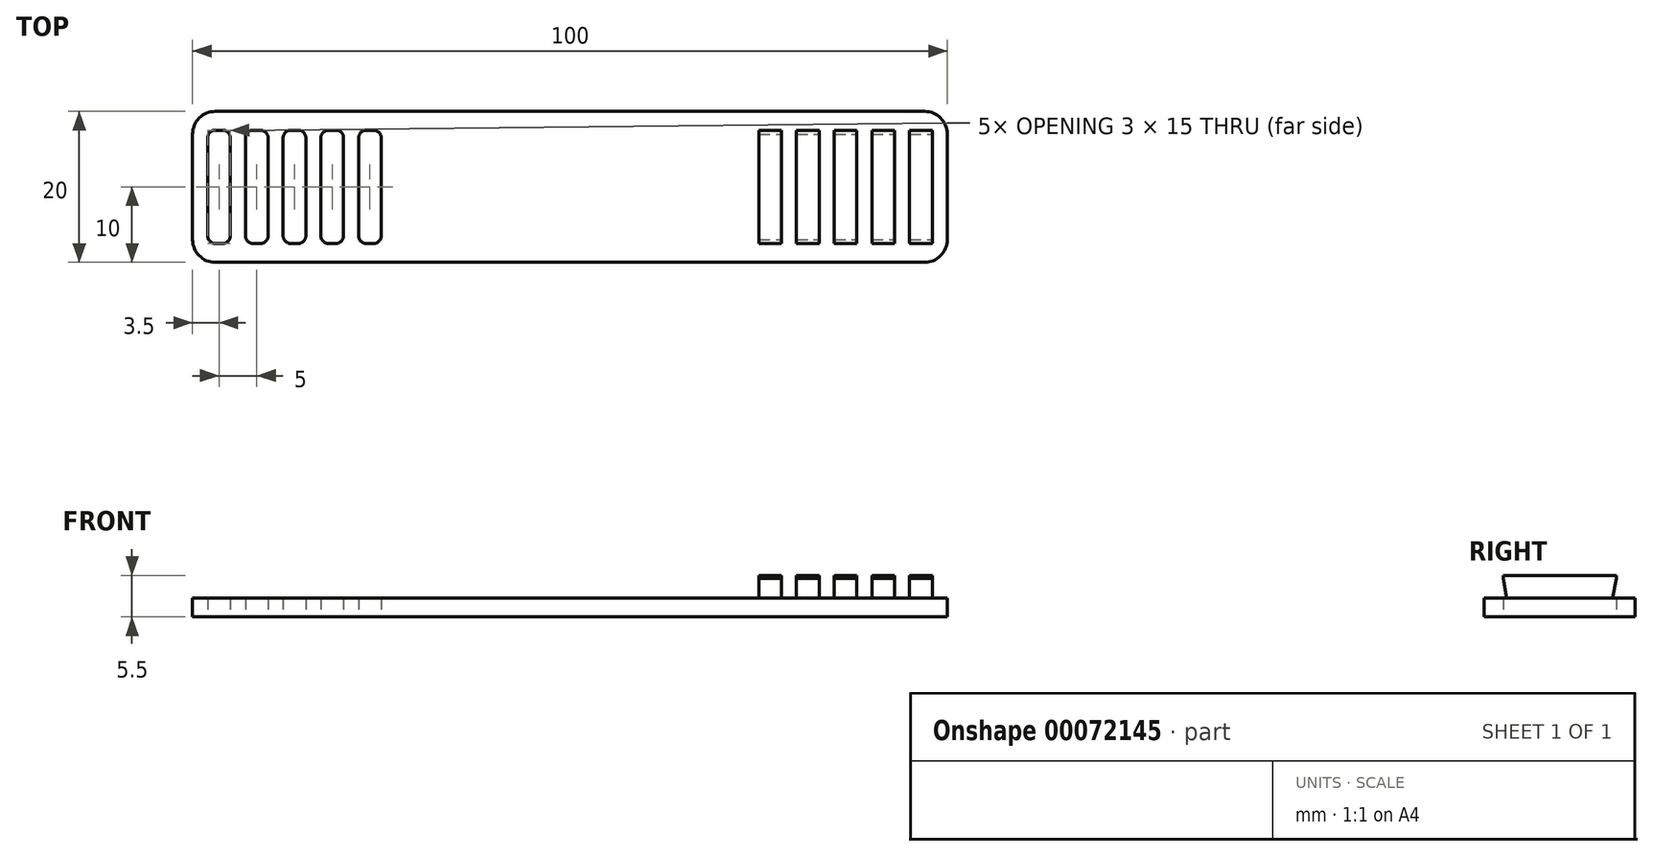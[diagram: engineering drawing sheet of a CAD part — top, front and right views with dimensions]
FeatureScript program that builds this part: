
annotation { "Feature Type Name" : "Feature", "Feature Type Description" : "" }
export const myFeature = defineFeature(function(context is Context, id is Id, definition is map)
    precondition{}
    {
        {
            var Q0;
            Q0=qCreatedBy(makeId("Top.planeOp"),FACE);
            var sketch = newSketch(context, id + "F0", { "sketchPlane" : qUnion([Q0])});
            skLineSegment(sketch, "E0.rect.bottom", {"start": v(50, -10) * mm, "end": v(-50, -10) * mm});
            skLineSegment(sketch, "E0.rect.top", {"start": v(50, 10) * mm, "end": v(-50, 10) * mm});
            skLineSegment(sketch, "E0.rect.left", {"start": v(50, -10) * mm, "end": v(50, 10) * mm});
            skLineSegment(sketch, "E0.rect.right", {"start": v(-50, -10) * mm, "end": v(-50, 10) * mm});
            skPoint(sketch, "E0.rect.middle", {"position": v(0, 0) * mm});
            skLineSegment(sketch, "E1", {"start": v(0, 10) * mm, "end": v(0, -10) * mm, "construction": true});
            skLineSegment(sketch, "E2", {"start": v(-50, 0) * mm, "end": v(50, 0) * mm, "construction": true});
            skLineSegment(sketch, "E3.rect.bottom", {"start": v(-46, -7.5) * mm, "end": v(-47, -7.5) * mm});
            skLineSegment(sketch, "E3.rect.top", {"start": v(-46, 7.5) * mm, "end": v(-47, 7.5) * mm});
            skLineSegment(sketch, "E3.rect.left", {"start": v(-45, -6.5) * mm, "end": v(-45, 6.5) * mm});
            skLineSegment(sketch, "E3.rect.right", {"start": v(-48, -6.5) * mm, "end": v(-48, 6.5) * mm});
            skPoint(sketch, "E3.rect.middle", {"position": v(-46.5, 0) * mm});
            skLineSegment(sketch, "E4.1.0.0", {"start": v(-41, 7.5) * mm, "end": v(-42, 7.5) * mm});
            skLineSegment(sketch, "E4.1.0.1", {"start": v(-40, -6.5) * mm, "end": v(-40, 6.5) * mm});
            skLineSegment(sketch, "E4.1.0.2", {"start": v(-41, -7.5) * mm, "end": v(-42, -7.5) * mm});
            skLineSegment(sketch, "E4.1.0.3", {"start": v(-43, -6.5) * mm, "end": v(-43, 6.5) * mm});
            skLineSegment(sketch, "E4.2.0.0", {"start": v(-36, 7.5) * mm, "end": v(-37, 7.5) * mm});
            skLineSegment(sketch, "E4.2.0.1", {"start": v(-35, -6.5) * mm, "end": v(-35, 6.5) * mm});
            skLineSegment(sketch, "E4.2.0.2", {"start": v(-36, -7.5) * mm, "end": v(-37, -7.5) * mm});
            skLineSegment(sketch, "E4.2.0.3", {"start": v(-38, -6.5) * mm, "end": v(-38, 6.5) * mm});
            skLineSegment(sketch, "E4.3.0.0", {"start": v(-31, 7.5) * mm, "end": v(-32, 7.5) * mm});
            skLineSegment(sketch, "E4.3.0.1", {"start": v(-30, -6.5) * mm, "end": v(-30, 6.5) * mm});
            skLineSegment(sketch, "E4.3.0.2", {"start": v(-31, -7.5) * mm, "end": v(-32, -7.5) * mm});
            skLineSegment(sketch, "E4.3.0.3", {"start": v(-33, -6.5) * mm, "end": v(-33, 6.5) * mm});
            skLineSegment(sketch, "E4.4.0.0", {"start": v(-26, 7.5) * mm, "end": v(-27, 7.5) * mm});
            skLineSegment(sketch, "E4.4.0.1", {"start": v(-25, -6.5) * mm, "end": v(-25, 6.5) * mm});
            skLineSegment(sketch, "E4.4.0.2", {"start": v(-26, -7.5) * mm, "end": v(-27, -7.5) * mm});
            skLineSegment(sketch, "E4.4.0.3", {"start": v(-28, -6.5) * mm, "end": v(-28, 6.5) * mm});
            skLineSegment(sketch, "E4.direction1", {"start": v(-48, 7.5) * mm, "end": v(-43, 7.5) * mm, "construction": true});
            skLineSegment(sketch, "E5.MirrorCS", {"start": v(48, 7.5) * mm, "end": v(43, 7.5) * mm, "construction": true});
            skLineSegment(sketch, "E6.MirrorCS", {"start": v(30, 7.5) * mm, "end": v(33, 7.5) * mm});
            skLineSegment(sketch, "E7.MirrorCS", {"start": v(25, 7.5) * mm, "end": v(28, 7.5) * mm});
            skLineSegment(sketch, "E8.MirrorCS", {"start": v(28, -7.5) * mm, "end": v(28, 7.5) * mm});
            skLineSegment(sketch, "E9.MirrorCS", {"start": v(38, -7.5) * mm, "end": v(38, 7.5) * mm});
            skLineSegment(sketch, "E10.MirrorCS", {"start": v(33, -7.5) * mm, "end": v(33, 7.5) * mm});
            skLineSegment(sketch, "E11.MirrorCS", {"start": v(25, -7.5) * mm, "end": v(28, -7.5) * mm});
            skPoint(sketch, "E12.MirrorP", {"position": v(46.5, 0) * mm});
            skLineSegment(sketch, "E13.MirrorCS", {"start": v(35, -7.5) * mm, "end": v(38, -7.5) * mm});
            skLineSegment(sketch, "E14.MirrorCS", {"start": v(30, -7.5) * mm, "end": v(33, -7.5) * mm});
            skLineSegment(sketch, "E15.MirrorCS", {"start": v(25, -7.5) * mm, "end": v(25, 7.5) * mm});
            skLineSegment(sketch, "E16.MirrorCS", {"start": v(40, -7.5) * mm, "end": v(43, -7.5) * mm});
            skLineSegment(sketch, "E17.MirrorCS", {"start": v(40, -7.5) * mm, "end": v(40, 7.5) * mm});
            skLineSegment(sketch, "E18.MirrorCS", {"start": v(40, 7.5) * mm, "end": v(43, 7.5) * mm});
            skLineSegment(sketch, "E19.MirrorCS", {"start": v(48, -7.5) * mm, "end": v(48, 7.5) * mm});
            skLineSegment(sketch, "E20.MirrorCS", {"start": v(45, -7.5) * mm, "end": v(45, 7.5) * mm});
            skLineSegment(sketch, "E21.MirrorCS", {"start": v(45, 7.5) * mm, "end": v(48, 7.5) * mm});
            skLineSegment(sketch, "E22.MirrorCS", {"start": v(45, -7.5) * mm, "end": v(48, -7.5) * mm});
            skLineSegment(sketch, "E23.MirrorCS", {"start": v(30, -7.5) * mm, "end": v(30, 7.5) * mm});
            skLineSegment(sketch, "E24.MirrorCS", {"start": v(43, -7.5) * mm, "end": v(43, 7.5) * mm});
            skLineSegment(sketch, "E25.MirrorCS", {"start": v(35, 7.5) * mm, "end": v(38, 7.5) * mm});
            skLineSegment(sketch, "E26.MirrorCS", {"start": v(35, -7.5) * mm, "end": v(35, 7.5) * mm});
            skPoint(sketch, "E27.visualSharp", {"position": v(-48, 7.5) * mm});
            skArc(sketch, "E27.filletArc", {"start": v(-47, 7.5) * mm, "mid": v(-47.7, 7.2) * mm, "end": v(-48, 6.5) * mm});
            skPoint(sketch, "E28.visualSharp", {"position": v(-45, 7.5) * mm});
            skArc(sketch, "E28.filletArc", {"start": v(-45, 6.5) * mm, "mid": v(-45.3, 7.2) * mm, "end": v(-46, 7.5) * mm});
            skPoint(sketch, "E29.visualSharp", {"position": v(-45, -7.5) * mm});
            skArc(sketch, "E29.filletArc", {"start": v(-46, -7.5) * mm, "mid": v(-45.3, -7.2) * mm, "end": v(-45, -6.5) * mm});
            skPoint(sketch, "E30.visualSharp", {"position": v(-48, -7.5) * mm});
            skArc(sketch, "E30.filletArc", {"start": v(-48, -6.5) * mm, "mid": v(-47.7, -7.2) * mm, "end": v(-47, -7.5) * mm});
            skPoint(sketch, "E31.visualSharp", {"position": v(-43, 7.5) * mm});
            skArc(sketch, "E31.filletArc", {"start": v(-42, 7.5) * mm, "mid": v(-42.7, 7.2) * mm, "end": v(-43, 6.5) * mm});
            skPoint(sketch, "E32.visualSharp", {"position": v(-40, 7.5) * mm});
            skArc(sketch, "E32.filletArc", {"start": v(-40, 6.5) * mm, "mid": v(-40.3, 7.2) * mm, "end": v(-41, 7.5) * mm});
            skPoint(sketch, "E33.visualSharp", {"position": v(-38, 7.5) * mm});
            skArc(sketch, "E33.filletArc", {"start": v(-37, 7.5) * mm, "mid": v(-37.7, 7.2) * mm, "end": v(-38, 6.5) * mm});
            skPoint(sketch, "E34.visualSharp", {"position": v(-35, 7.5) * mm});
            skArc(sketch, "E34.filletArc", {"start": v(-35, 6.5) * mm, "mid": v(-35.3, 7.2) * mm, "end": v(-36, 7.5) * mm});
            skPoint(sketch, "E35.visualSharp", {"position": v(-33, 7.5) * mm});
            skArc(sketch, "E35.filletArc", {"start": v(-32, 7.5) * mm, "mid": v(-32.7, 7.2) * mm, "end": v(-33, 6.5) * mm});
            skPoint(sketch, "E36.visualSharp", {"position": v(-30, 7.5) * mm});
            skArc(sketch, "E36.filletArc", {"start": v(-30, 6.5) * mm, "mid": v(-30.3, 7.2) * mm, "end": v(-31, 7.5) * mm});
            skPoint(sketch, "E37.visualSharp", {"position": v(-28, 7.5) * mm});
            skArc(sketch, "E37.filletArc", {"start": v(-27, 7.5) * mm, "mid": v(-27.7, 7.2) * mm, "end": v(-28, 6.5) * mm});
            skPoint(sketch, "E38.visualSharp", {"position": v(-25, 7.5) * mm});
            skArc(sketch, "E38.filletArc", {"start": v(-25, 6.5) * mm, "mid": v(-25.3, 7.2) * mm, "end": v(-26, 7.5) * mm});
            skPoint(sketch, "E39.visualSharp", {"position": v(-25, -7.5) * mm});
            skArc(sketch, "E39.filletArc", {"start": v(-26, -7.5) * mm, "mid": v(-25.3, -7.2) * mm, "end": v(-25, -6.5) * mm});
            skPoint(sketch, "E40.visualSharp", {"position": v(-28, -7.5) * mm});
            skArc(sketch, "E40.filletArc", {"start": v(-28, -6.5) * mm, "mid": v(-27.7, -7.2) * mm, "end": v(-27, -7.5) * mm});
            skPoint(sketch, "E41.visualSharp", {"position": v(-30, -7.5) * mm});
            skArc(sketch, "E41.filletArc", {"start": v(-31, -7.5) * mm, "mid": v(-30.3, -7.2) * mm, "end": v(-30, -6.5) * mm});
            skPoint(sketch, "E42.visualSharp", {"position": v(-33, -7.5) * mm});
            skArc(sketch, "E42.filletArc", {"start": v(-33, -6.5) * mm, "mid": v(-32.7, -7.2) * mm, "end": v(-32, -7.5) * mm});
            skPoint(sketch, "E43.visualSharp", {"position": v(-35, -7.5) * mm});
            skArc(sketch, "E43.filletArc", {"start": v(-36, -7.5) * mm, "mid": v(-35.3, -7.2) * mm, "end": v(-35, -6.5) * mm});
            skPoint(sketch, "E44.visualSharp", {"position": v(-38, -7.5) * mm});
            skArc(sketch, "E44.filletArc", {"start": v(-38, -6.5) * mm, "mid": v(-37.7, -7.2) * mm, "end": v(-37, -7.5) * mm});
            skPoint(sketch, "E45.visualSharp", {"position": v(-40, -7.5) * mm});
            skArc(sketch, "E45.filletArc", {"start": v(-41, -7.5) * mm, "mid": v(-40.3, -7.2) * mm, "end": v(-40, -6.5) * mm});
            skPoint(sketch, "E46.visualSharp", {"position": v(-43, -7.5) * mm});
            skArc(sketch, "E46.filletArc", {"start": v(-43, -6.5) * mm, "mid": v(-42.7, -7.2) * mm, "end": v(-42, -7.5) * mm});
            skSolve(sketch);
        }
        {
            var Q0;
            Q0=makeQuery(id+"F0.imprint","IMPRINT",FACE,{"disambiguationData":[TD([[makeQuery(id+"F0.imprint","IMPRINT",EDGE,{"derivedFrom":sQuery(id+"F0.wireOp",EDGE,"E0.rect.bottom")}),-1.0]])]});
            var Q1;
            Q1=makeQuery(id+"F0.imprint","IMPRINT",FACE,{"disambiguationData":[TD([[makeQuery(id+"F0.imprint","IMPRINT",EDGE,{"derivedFrom":sQuery(id+"F0.wireOp",EDGE,"bae3096f-2a75-4a92-8632-1d8423ab57ea2.MirrorCS")}),-1.0]])]});
            var Q2;
            Q2=makeQuery(id+"F0.imprint","IMPRINT",FACE,{"disambiguationData":[TD([[makeQuery(id+"F0.imprint","IMPRINT",EDGE,{"derivedFrom":sQuery(id+"F0.wireOp",EDGE,"E60.MirrorCS")}),1.0]])]});
            var Q3;
            Q3=makeQuery(id+"F0.imprint","IMPRINT",FACE,{"disambiguationData":[TD([[makeQuery(id+"F0.imprint","IMPRINT",EDGE,{"derivedFrom":sQuery(id+"F0.wireOp",EDGE,"E7.MirrorCS")}),-1.0]])]});
            var Q4;
            Q4=makeQuery(id+"F0.imprint","IMPRINT",FACE,{"disambiguationData":[TD([[makeQuery(id+"F0.imprint","IMPRINT",EDGE,{"derivedFrom":sQuery(id+"F0.wireOp",EDGE,"E6.MirrorCS")}),-1.0]])]});
            var Q5;
            Q5=makeQuery(id+"F0.imprint","IMPRINT",FACE,{"disambiguationData":[TD([[makeQuery(id+"F0.imprint","IMPRINT",EDGE,{"derivedFrom":sQuery(id+"F0.wireOp",EDGE,"E9.MirrorCS")}),1.0]])]});
            var Q6;
            Q6=makeQuery(id+"F0.imprint","IMPRINT",FACE,{"disambiguationData":[TD([[makeQuery(id+"F0.imprint","IMPRINT",EDGE,{"derivedFrom":sQuery(id+"F0.wireOp",EDGE,"E16.MirrorCS")}),1.0]])]});
            var Q7;
            Q7=makeQuery(id+"F0.imprint","IMPRINT",FACE,{"disambiguationData":[TD([[makeQuery(id+"F0.imprint","IMPRINT",EDGE,{"derivedFrom":sQuery(id+"F0.wireOp",EDGE,"E19.MirrorCS")}),1.0]])]});
            extrude(context, id + "F1", {"entities" : qUnion([Q0, Q1, Q2, Q3, Q4, Q5, Q6, Q7]), "depth" : 2.5 * mm});
        }
        {
            var Q0;
            Q0=makeQuery(id+"F1.opExtrude","CAP_FACE",FACE,{"disambiguationData":[OSD([sQuery(id+"F0.wireOp",EDGE,"E0.rect.bottom"),sQuery(id+"F0.wireOp",EDGE,"E0.rect.top"),sQuery(id+"F0.wireOp",EDGE,"E0.rect.left"),sQuery(id+"F0.wireOp",EDGE,"E0.rect.right"),sQuery(id+"F0.wireOp",EDGE,"E3.rect.bottom"),sQuery(id+"F0.wireOp",EDGE,"E3.rect.top"),sQuery(id+"F0.wireOp",EDGE,"E3.rect.left"),sQuery(id+"F0.wireOp",EDGE,"E3.rect.right"),sQuery(id+"F0.wireOp",EDGE,"E4.1.0.0"),sQuery(id+"F0.wireOp",EDGE,"E4.1.0.1"),sQuery(id+"F0.wireOp",EDGE,"E4.1.0.2"),sQuery(id+"F0.wireOp",EDGE,"E4.1.0.3"),sQuery(id+"F0.wireOp",EDGE,"E4.2.0.0"),sQuery(id+"F0.wireOp",EDGE,"E4.2.0.1"),sQuery(id+"F0.wireOp",EDGE,"E4.2.0.2"),sQuery(id+"F0.wireOp",EDGE,"E4.2.0.3"),sQuery(id+"F0.wireOp",EDGE,"E4.3.0.0"),sQuery(id+"F0.wireOp",EDGE,"E4.3.0.1"),sQuery(id+"F0.wireOp",EDGE,"E4.3.0.2"),sQuery(id+"F0.wireOp",EDGE,"E4.3.0.3"),sQuery(id+"F0.wireOp",EDGE,"E4.4.0.0"),sQuery(id+"F0.wireOp",EDGE,"E4.4.0.1"),sQuery(id+"F0.wireOp",EDGE,"E4.4.0.2"),sQuery(id+"F0.wireOp",EDGE,"E4.4.0.3")])],"isStart":false});
            var sketch = newSketch(context, id + "F2", { "sketchPlane" : qUnion([Q0])});
            skLineSegment(sketch, "E47.0", {"start": v(-46, 7.5) * mm, "end": v(-46, 7.5) * mm});
            skLineSegment(sketch, "E48.0", {"start": v(-48, -6.5) * mm, "end": v(-48, 7.5) * mm});
            skLineSegment(sketch, "E49.0", {"start": v(-45, -6.5) * mm, "end": v(-45, 7.5) * mm});
            skLineSegment(sketch, "E50.0", {"start": v(-45, -7.5) * mm, "end": v(-48, -7.5) * mm});
            skLineSegment(sketch, "E51.0", {"start": v(-41, -7.5) * mm, "end": v(-41, -7.5) * mm});
            skLineSegment(sketch, "E52.0", {"start": v(-36, -7.5) * mm, "end": v(-36, -7.5) * mm});
            skLineSegment(sketch, "E53.0", {"start": v(-31, -7.5) * mm, "end": v(-31, -7.5) * mm});
            skLineSegment(sketch, "E54.0", {"start": v(-26, -7.5) * mm, "end": v(-26, -7.5) * mm});
            skLineSegment(sketch, "E55.0", {"start": v(-26, 7.5) * mm, "end": v(-26, 7.5) * mm});
            skLineSegment(sketch, "E56.0", {"start": v(-31, 7.5) * mm, "end": v(-31, 7.5) * mm});
            skLineSegment(sketch, "E57.0", {"start": v(-36, 7.5) * mm, "end": v(-36, 7.5) * mm});
            skLineSegment(sketch, "E58.0", {"start": v(-41, 7.5) * mm, "end": v(-41, 7.5) * mm});
            skLineSegment(sketch, "E59.0", {"start": v(-43, -7.5) * mm, "end": v(-43, 7.5) * mm});
            skLineSegment(sketch, "E60.0", {"start": v(-40, -7.5) * mm, "end": v(-40, 7.5) * mm});
            skLineSegment(sketch, "E61.0", {"start": v(-38, -7.5) * mm, "end": v(-38, 7.5) * mm});
            skLineSegment(sketch, "E62.0", {"start": v(-35, -7.5) * mm, "end": v(-35, 7.5) * mm});
            skLineSegment(sketch, "E63.0", {"start": v(-33, -7.5) * mm, "end": v(-33, 7.5) * mm});
            skLineSegment(sketch, "E64.0", {"start": v(-30, -7.5) * mm, "end": v(-30, 7.5) * mm});
            skLineSegment(sketch, "E65.0", {"start": v(-28, -7.5) * mm, "end": v(-28, 7.5) * mm});
            skLineSegment(sketch, "E66.0", {"start": v(-25, -7.5) * mm, "end": v(-25, 7.5) * mm});
            skLineSegment(sketch, "E67.0", {"start": v(50, 10) * mm, "end": v(-50, 10) * mm});
            skLineSegment(sketch, "E68", {"start": v(0, 10) * mm, "end": v(0, -10) * mm, "construction": true});
            skLineSegment(sketch, "E69.MirrorCS", {"start": v(30, -7.5) * mm, "end": v(33, -7.5) * mm});
            skLineSegment(sketch, "E70.MirrorCS", {"start": v(25, -7.5) * mm, "end": v(28, -7.5) * mm});
            skLineSegment(sketch, "E71.MirrorCS", {"start": v(35, -7.5) * mm, "end": v(38, -7.5) * mm});
            skLineSegment(sketch, "E72.MirrorCS", {"start": v(40, -7.5) * mm, "end": v(43, -7.5) * mm});
            skLineSegment(sketch, "E73.MirrorCS", {"start": v(25, 7.5) * mm, "end": v(28, 7.5) * mm});
            skLineSegment(sketch, "E74.MirrorCS", {"start": v(45, -7.5) * mm, "end": v(48, -7.5) * mm});
            skLineSegment(sketch, "E75.MirrorCS", {"start": v(30, 7.5) * mm, "end": v(33, 7.5) * mm});
            skLineSegment(sketch, "E76.MirrorCS", {"start": v(45, -7.5) * mm, "end": v(45, 7.5) * mm});
            skLineSegment(sketch, "E77.MirrorCS", {"start": v(48, -7.5) * mm, "end": v(48, 7.5) * mm});
            skLineSegment(sketch, "E78.MirrorCS", {"start": v(35, 7.5) * mm, "end": v(38, 7.5) * mm});
            skLineSegment(sketch, "E79.MirrorCS", {"start": v(45, 7.5) * mm, "end": v(48, 7.5) * mm});
            skLineSegment(sketch, "E80.MirrorCS", {"start": v(40, 7.5) * mm, "end": v(43, 7.5) * mm});
            skLineSegment(sketch, "E81.MirrorCS", {"start": v(35, -7.5) * mm, "end": v(35, 7.5) * mm});
            skLineSegment(sketch, "E82.MirrorCS", {"start": v(38, -7.5) * mm, "end": v(38, 7.5) * mm});
            skLineSegment(sketch, "E83.MirrorCS", {"start": v(43, -7.5) * mm, "end": v(43, 7.5) * mm});
            skLineSegment(sketch, "E84.MirrorCS", {"start": v(40, -7.5) * mm, "end": v(40, 7.5) * mm});
            skLineSegment(sketch, "E85.MirrorCS", {"start": v(25, -7.5) * mm, "end": v(25, 7.5) * mm});
            skLineSegment(sketch, "E86.MirrorCS", {"start": v(33, -7.5) * mm, "end": v(33, 7.5) * mm});
            skLineSegment(sketch, "E87.MirrorCS", {"start": v(30, -7.5) * mm, "end": v(30, 7.5) * mm});
            skLineSegment(sketch, "E88.MirrorCS", {"start": v(28, -7.5) * mm, "end": v(28, 7.5) * mm});
            skSolve(sketch);
        }
        {
            var Q0;
            Q0=makeQuery(id+"F2.imprint","IMPRINT",FACE,{"disambiguationData":[TD([[makeQuery(id+"F2.imprint","IMPRINT",EDGE,{"derivedFrom":sQuery(id+"F2.wireOp",EDGE,"E70.MirrorCS")}),1.0]])]});
            var Q1;
            Q1=makeQuery(id+"F2.imprint","IMPRINT",FACE,{"disambiguationData":[TD([[makeQuery(id+"F2.imprint","IMPRINT",EDGE,{"derivedFrom":sQuery(id+"F2.wireOp",EDGE,"E69.MirrorCS")}),1.0]])]});
            var Q2;
            Q2=makeQuery(id+"F2.imprint","IMPRINT",FACE,{"disambiguationData":[TD([[makeQuery(id+"F2.imprint","IMPRINT",EDGE,{"derivedFrom":sQuery(id+"F2.wireOp",EDGE,"E71.MirrorCS")}),1.0]])]});
            var Q3;
            Q3=makeQuery(id+"F2.imprint","IMPRINT",FACE,{"disambiguationData":[TD([[makeQuery(id+"F2.imprint","IMPRINT",EDGE,{"derivedFrom":sQuery(id+"F2.wireOp",EDGE,"E72.MirrorCS")}),1.0]])]});
            var Q4;
            Q4=makeQuery(id+"F2.imprint","IMPRINT",FACE,{"disambiguationData":[TD([[makeQuery(id+"F2.imprint","IMPRINT",EDGE,{"derivedFrom":sQuery(id+"F2.wireOp",EDGE,"E74.MirrorCS")}),1.0]])]});
            extrude(context, id + "F3", {"entities" : qUnion([Q0, Q1, Q2, Q3, Q4]), "operationType" : NewBodyOperationType.ADD, "depth" : 3 * mm});
        }
        {
            var Q0;
            Q0=makeQuery(id+"F3.opExtrude","SWEPT_FACE",FACE,{"disambiguationData":[OSD([sQuery(id+"F2.wireOp",EDGE,"E77.MirrorCS")])]});
            var sketch = newSketch(context, id + "F4", { "sketchPlane" : qUnion([Q0])});
            skLineSegment(sketch, "E89.0.0", {"start": v(-7.5, 2.5) * mm, "end": v(7.5, 2.5) * mm});
            skLineSegment(sketch, "E89.0.1", {"start": v(7.5, 2.5) * mm, "end": v(7.5, 5.5) * mm});
            skLineSegment(sketch, "E89.0.2", {"start": v(7.5, 5.5) * mm, "end": v(-7.5, 5.5) * mm});
            skLineSegment(sketch, "E89.0.3", {"start": v(-7.5, 5.5) * mm, "end": v(-7.5, 2.5) * mm});
            skLineSegment(sketch, "E90", {"start": v(-7.5, 5.1) * mm, "end": v(7.5, 5.1) * mm, "construction": true});
            skLineSegment(sketch, "E91", {"start": v(-7.5, 5.1) * mm, "end": v(-7, 2.5) * mm});
            skLineSegment(sketch, "E92", {"start": v(7.5, 5.1) * mm, "end": v(7, 2.5) * mm});
            skSolve(sketch);
        }
        {
            var Q0;
            {var subQ3=sQuery(id+"F4.wireOp",EDGE,"E91");Q0=makeQuery(id+"F4.imprint","IMPRINT",FACE,{"disambiguationData":[TD([[makeQuery(id+"F4.imprint","IMPRINT",EDGE,{"derivedFrom":subQ3}),-1.0]])]});}
            var Q1;
            {var subQ3=sQuery(id+"F4.wireOp",EDGE,"E92");Q1=makeQuery(id+"F4.imprint","IMPRINT",FACE,{"disambiguationData":[TD([[makeQuery(id+"F4.imprint","IMPRINT",EDGE,{"derivedFrom":subQ3}),1.0]])]});}
            extrude(context, id + "F5", {"entities" : qUnion([Q0, Q1]), "operationType" : NewBodyOperationType.REMOVE, "endBound" : BoundingType.THROUGH_ALL, "oppositeDirection" : true, "depth" : 25 * mm});
        }
        {
            var Q0;
            Q0=makeQuery(id+"F1.opExtrude","SWEPT_EDGE",EDGE,{"disambiguationData":[OSD([sQuery(id+"F0.wireOp",EDGE,"E0.rect.bottom"),sQuery(id+"F0.wireOp",EDGE,"E0.rect.right")])]});
            var Q1;
            Q1=makeQuery(id+"F1.opExtrude","SWEPT_EDGE",EDGE,{"disambiguationData":[OSD([sQuery(id+"F0.wireOp",EDGE,"E0.rect.bottom"),sQuery(id+"F0.wireOp",EDGE,"E0.rect.left")])]});
            var Q2;
            Q2=makeQuery(id+"F1.opExtrude","SWEPT_EDGE",EDGE,{"disambiguationData":[OSD([sQuery(id+"F0.wireOp",EDGE,"E0.rect.top"),sQuery(id+"F0.wireOp",EDGE,"E0.rect.right")])]});
            var Q3;
            Q3=makeQuery(id+"F1.opExtrude","SWEPT_EDGE",EDGE,{"disambiguationData":[OSD([sQuery(id+"F0.wireOp",EDGE,"E0.rect.top"),sQuery(id+"F0.wireOp",EDGE,"E0.rect.left")])]});
            fillet(context, id + "F6", {"entities" : qUnion([Q0, Q1, Q2, Q3]), "radius" : 3 * mm, "tangentPropagation" : true, "allowEdgeOverflow" : false});
        }
    });
